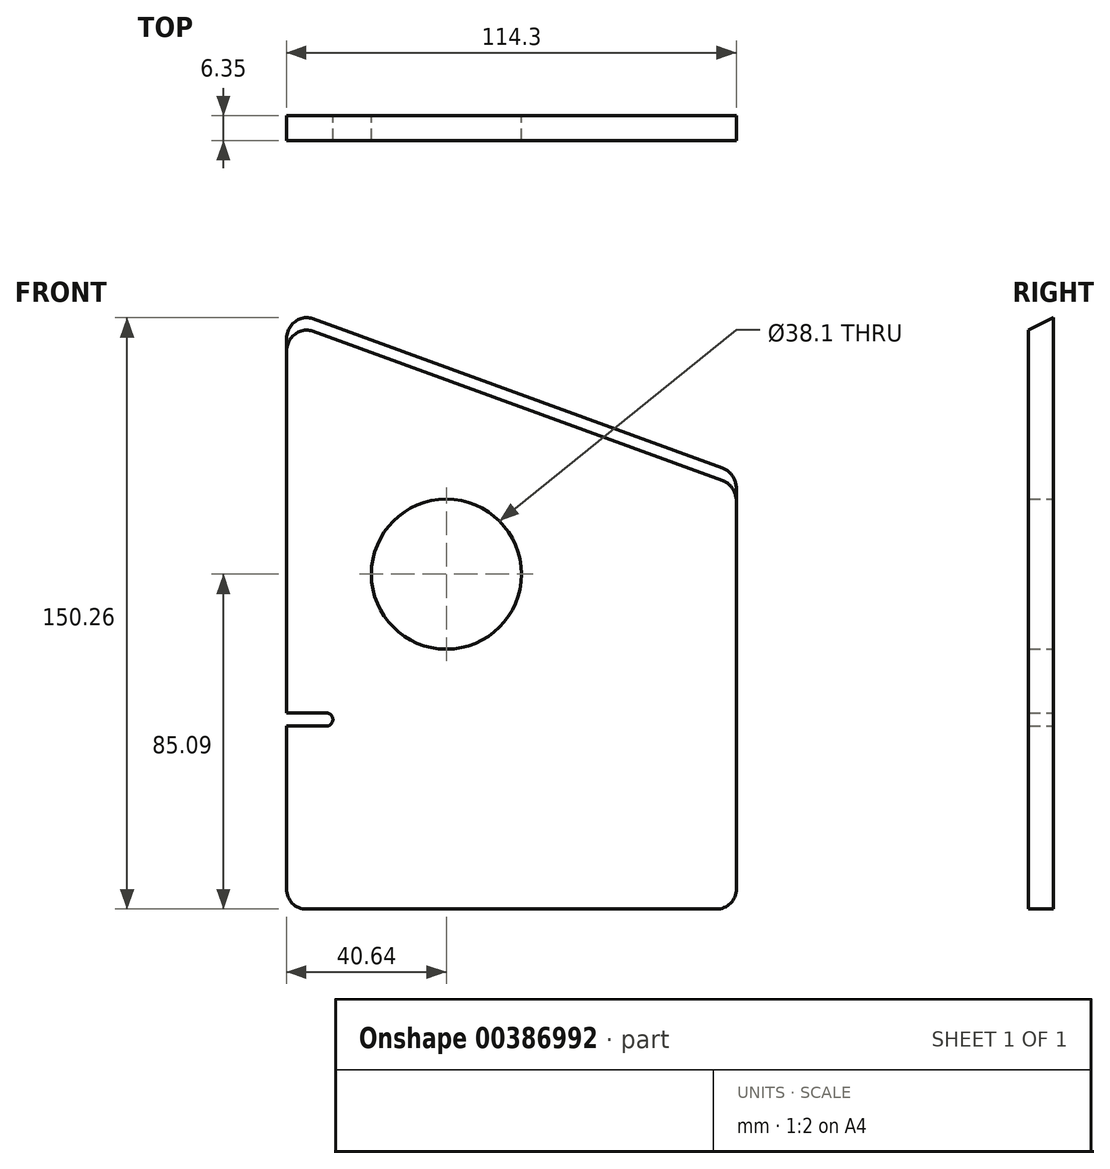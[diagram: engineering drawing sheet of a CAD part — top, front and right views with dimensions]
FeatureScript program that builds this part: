
annotation { "Feature Type Name" : "Feature", "Feature Type Description" : "" }
export const myFeature = defineFeature(function(context is Context, id is Id, definition is map)
    precondition{}
    {
        {
            var Q0;
            Q0=qCreatedBy(makeId("Front.planeOp"),FACE);
            var sketch = newSketch(context, id + "F0", { "sketchPlane" : qUnion([Q0])});
            skLineSegment(sketch, "E0", {"start": v(0, 0) * mm, "end": v(0, 46.5) * mm});
            skLineSegment(sketch, "E1", {"start": v(0, 152.4) * mm, "end": v(114.3, 110.8) * mm});
            skLineSegment(sketch, "E2", {"start": v(114.3, 110.8) * mm, "end": v(114.3, 0) * mm});
            skLineSegment(sketch, "E3", {"start": v(114.3, 0) * mm, "end": v(0, 0) * mm});
            skCircle(sketch, "E4", {"center": v(40.64, 85.1) * mm, "radius": 19.05 * mm});
            skLineSegment(sketch, "E5.bottom", {"start": v(0, 49.81) * mm, "end": v(10.16, 49.81) * mm});
            skLineSegment(sketch, "E5.top", {"start": v(0, 46.5) * mm, "end": v(10.16, 46.5) * mm});
            skArc(sketch, "E6", {"start": v(10.16, 46.5) * mm, "mid": v(11.81, 48.16) * mm, "end": v(10.16, 49.81) * mm});
            skLineSegment(sketch, "E7.trimOffspring", {"start": v(0, 49.81) * mm, "end": v(0, 152.4) * mm});
            skSolve(sketch);
        }
        {
            var Q0;
            Q0=makeQuery(id+"F0.imprint","IMPRINT",FACE,{"disambiguationData":[TD([[makeQuery(id+"F0.imprint","IMPRINT",EDGE,{"derivedFrom":sQuery(id+"F0.wireOp",EDGE,"E0")}),-1.0]])]});
            extrude(context, id + "F1", {"entities" : qUnion([Q0]), "depth" : 6.35 * mm});
        }
        {
            var Q0;
            Q0=makeQuery(id+"F1.opExtrude","SWEPT_FACE",FACE,{"disambiguationData":[OSD([sQuery(id+"F0.wireOp",EDGE,"E1")])]});
            var Q1;
            Q1=makeQuery(id+"F1.opExtrude","SWEPT_EDGE",EDGE,{"disambiguationData":[OSD([sQuery(id+"F0.wireOp",EDGE,"E1"),sQuery(id+"F0.wireOp",EDGE,"E7.trimOffspring")])]});
            cPlane(context, id + "F2", {"entities" : qUnion([Q0, Q1]), "cplaneType" : CPlaneType.LINE_ANGLE, "offset" : 25.4 * mm, "angle" : 90 * degree, "width" : 152.4 * mm, "height" : 152.4 * mm});
        }
        {
            var Q0;
            Q0=qCreatedBy(id+"F2.planeOp",FACE);
            var sketch = newSketch(context, id + "F3", { "sketchPlane" : qUnion([Q0])});
            skLineSegment(sketch, "E8.0.0", {"start": v(0, 143.2) * mm, "end": v(0, 46.8) * mm});
            skLineSegment(sketch, "E8.0.1", {"start": v(0, 46.8) * mm, "end": v(6.35, 46.8) * mm});
            skLineSegment(sketch, "E8.0.2", {"start": v(6.35, 46.8) * mm, "end": v(6.35, 143.2) * mm});
            skLineSegment(sketch, "E8.0.3", {"start": v(6.35, 143.2) * mm, "end": v(0, 143.2) * mm});
            skLineSegment(sketch, "E9", {"start": v(0, 143.2) * mm, "end": v(6.35, 140.25) * mm});
            skLineSegment(sketch, "E10", {"start": v(6.35, 140.25) * mm, "end": v(6.35, 143.2) * mm});
            skSolve(sketch);
        }
        {
            var Q0;
            Q0=makeQuery(id+"F3.imprint","IMPRINT",FACE,{"disambiguationData":[TD([[makeQuery(id+"F3.imprint","IMPRINT",EDGE,{"derivedFrom":sQuery(id+"F3.wireOp",EDGE,"E9")}),1.0]])]});
            extrude(context, id + "F4", {"entities" : qUnion([Q0]), "operationType" : NewBodyOperationType.REMOVE, "endBound" : BoundingType.THROUGH_ALL, "oppositeDirection" : true, "depth" : 123.95 * mm});
        }
        {
            var Q0;
            Q0=makeQuery(id+"F4.boolean.opBoolean","INTERSECT",EDGE,{"derivedFrom":[makeQuery(id+"F1.opExtrude","SWEPT_FACE",FACE,{"disambiguationData":[OSD([sQuery(id+"F0.wireOp",EDGE,"E7.trimOffspring")])]}),makeQuery(id+"F4.opExtrude","SWEPT_FACE",FACE,{"disambiguationData":[OSD([sQuery(id+"F3.wireOp",EDGE,"E9")])]})]});
            var Q1;
            Q1=makeQuery(id+"F4.boolean.opBoolean","INTERSECT",EDGE,{"derivedFrom":[makeQuery(id+"F1.opExtrude","SWEPT_FACE",FACE,{"disambiguationData":[OSD([sQuery(id+"F0.wireOp",EDGE,"E2")])]}),makeQuery(id+"F4.opExtrude","SWEPT_FACE",FACE,{"disambiguationData":[OSD([sQuery(id+"F3.wireOp",EDGE,"E9")])]})]});
            var Q2;
            Q2=makeQuery(id+"F1.opExtrude","SWEPT_EDGE",EDGE,{"disambiguationData":[OSD([sQuery(id+"F0.wireOp",EDGE,"E2"),sQuery(id+"F0.wireOp",EDGE,"E3")])]});
            var Q3;
            Q3=makeQuery(id+"F1.opExtrude","SWEPT_EDGE",EDGE,{"disambiguationData":[OSD([sQuery(id+"F0.wireOp",EDGE,"E0"),sQuery(id+"F0.wireOp",EDGE,"E3")])]});
            fillet(context, id + "F5", {"entities" : qUnion([Q0, Q1, Q2, Q3]), "radius" : 5.08 * mm, "tangentPropagation" : true, "allowEdgeOverflow" : false});
        }
    });
